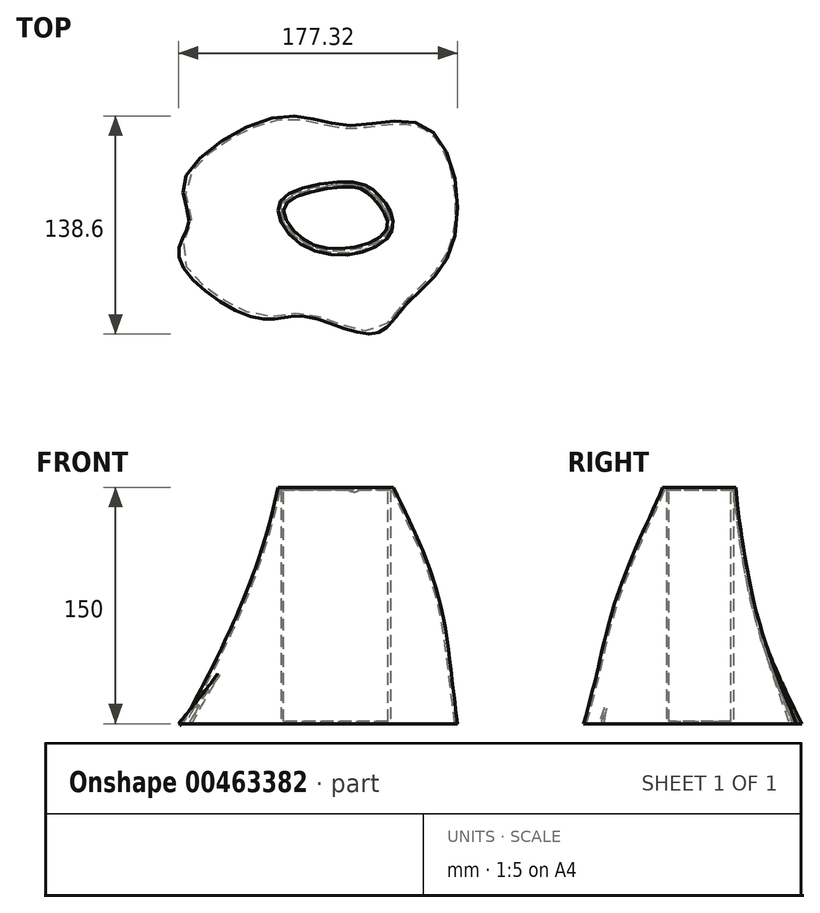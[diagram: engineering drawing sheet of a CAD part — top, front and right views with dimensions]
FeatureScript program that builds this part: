
annotation { "Feature Type Name" : "Feature", "Feature Type Description" : "" }
export const myFeature = defineFeature(function(context is Context, id is Id, definition is map)
    precondition{}
    {
        {
            var Q0;
            Q0=qCreatedBy(makeId("Top.planeOp"),FACE);
            var sketch = newSketch(context, id + "F0", { "sketchPlane" : qUnion([Q0])});
            skFitSpline(sketch, "E0", {"points": [v(-66.33, -68.2) * mm, v(-115.86, -29.77) * mm, v(-109.52, -7.19) * mm, v(-112.69, 18.96) * mm, v(-52.07, 59.77) * mm, v(-8.48, 54.23) * mm, v(43.42, 51.85) * mm, v(57.69, -22.64) * mm, v(27.97, -59.89) * mm, v(7.76, -78.11) * mm, v(-35.82, -67.02) * mm, v(-66.33, -68.2) * mm]});
            skSolve(sketch);
        }
        {
            var Q0;
            Q0=qCreatedBy(makeId("Top.planeOp"),FACE);
            cPlane(context, id + "F1", {"entities" : qUnion([Q0]), "cplaneType" : CPlaneType.OFFSET, "offset" : 70 * mm, "width" : 150 * mm, "height" : 150 * mm});
        }
        {
            var Q0;
            Q0=qCreatedBy(id+"F1.planeOp",FACE);
            var sketch = newSketch(context, id + "F2", { "sketchPlane" : qUnion([Q0])});
            skFitSpline(sketch, "E1", {"points": [v(-67.66, -20.3) * mm, v(-77.77, 18.13) * mm, v(-32.4, 30.8) * mm, v(37.14, 22.88) * mm, v(48.23, -24.47) * mm, v(-10.2, -59.73) * mm, v(-61.92, -23.28) * mm, v(-67.66, -20.3) * mm]});
            skSolve(sketch);
        }
        {
            var Q0;
            Q0=qCreatedBy(id+"F1.planeOp",FACE);
            cPlane(context, id + "F3", {"entities" : qUnion([Q0]), "cplaneType" : CPlaneType.OFFSET, "offset" : 80 * mm, "width" : 150 * mm, "height" : 150 * mm});
        }
        {
            var Q0;
            Q0=qCreatedBy(id+"F3.planeOp",FACE);
            var sketch = newSketch(context, id + "F4", { "sketchPlane" : qUnion([Q0])});
            skFitSpline(sketch, "E2", {"points": [v(-52.98, 0) * mm, v(-41.84, 12.83) * mm, v(-1.96, 17.7) * mm, v(9.98, 11.01) * mm, v(18.28, 0) * mm, v(19.3, -13.28) * mm, v(0, -26.44) * mm, v(-36.78, -22.19) * mm, v(-52.98, 0) * mm]});
            skPoint(sketch, "E3.1.internal.orphan", {"position": v(-46.5, 0) * mm});
            skPoint(sketch, "E3.5.internal.orphan", {"position": v(0, -20.97) * mm});
            skSolve(sketch);
        }
        {
            var Q0;
            Q0=makeQuery(id+"F4.imprint","IMPRINT",FACE,{"disambiguationData":[TD([[makeQuery(id+"F4.imprint","IMPRINT",EDGE,{"derivedFrom":sQuery(id+"F4.wireOp",EDGE,"E2")}),-1.0]])]});
            var Q1;
            Q1=makeQuery(id+"F2.imprint","IMPRINT",FACE,{"disambiguationData":[TD([[makeQuery(id+"F2.imprint","IMPRINT",EDGE,{"derivedFrom":sQuery(id+"F2.wireOp",EDGE,"E1")}),-1.0]])]});
            var Q2;
            Q2=makeQuery(id+"F0.imprint","IMPRINT",FACE,{"disambiguationData":[TD([[makeQuery(id+"F0.imprint","IMPRINT",EDGE,{"derivedFrom":sQuery(id+"F0.wireOp",EDGE,"E0")}),-1.0]])]});
            loft(context, id + "F5", {"sheetProfilesArray" : [{ "sheetProfileEntities" : qUnion([Q0]) }, { "sheetProfileEntities" : qUnion([Q1]) }, { "sheetProfileEntities" : qUnion([Q2]) }]});
        }
        {
            var Q0;
            Q0=qCreatedBy(id+"F3.planeOp",FACE);
            var sketch = newSketch(context, id + "F6", { "sketchPlane" : qUnion([Q0])});
            skPoint(sketch, "E4.1.internal.orphan", {"position": v(-44.27, 0) * mm});
            skPoint(sketch, "E4.7.internal.orphan", {"position": v(0, -17.33) * mm});
            skFitSpline(sketch, "E5", {"points": [v(-49.33, 0) * mm, v(-40.43, 9.2) * mm, v(-9.65, 15.26) * mm, v(0, 13.85) * mm, v(6.95, 8.58) * mm, v(13.63, 0) * mm, v(16.66, -10.04) * mm, v(5.73, -20.16) * mm, v(-21.8, -23.6) * mm, v(-39.82, -15.5) * mm, v(-49.33, 0) * mm]});
            skSolve(sketch);
        }
        {
            var Q0;
            Q0 = qSketchRegion(id + "F6", true);
            var Q1;
            Q1=makeQuery(id+"F4.imprint","IMPRINT",FACE,{"disambiguationData":[TD([[makeQuery(id+"F4.imprint","IMPRINT",EDGE,{"derivedFrom":sQuery(id+"F4.wireOp",EDGE,"E3")}),-1.0]])]});
            extrude(context, id + "F7", {"entities" : qUnion([Q0, Q1]), "operationType" : NewBodyOperationType.REMOVE, "oppositeDirection" : true, "depth" : 148.4 * mm});
        }
        {
            var Q0;
            Q0=makeQuery(id+"F5.opLoft","CAP_FACE",FACE,{"disambiguationData":[OSD([makeQuery(id+"F0.imprint","IMPRINT",FACE,{"disambiguationData":[TD([[makeQuery(id+"F0.imprint","IMPRINT",EDGE,{"derivedFrom":sQuery(id+"F0.wireOp",EDGE,"E0")}),-1.0]])]})])],"isStart":true});
            shell(context, id + "F8", {"entities" : qUnion([Q0]), "thickness" : 1.6 * mm});
        }
    });
